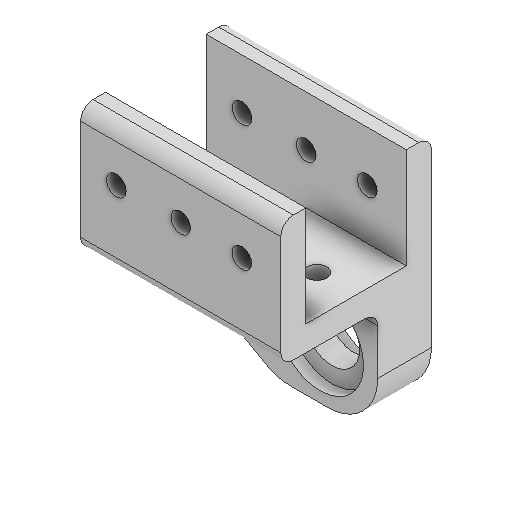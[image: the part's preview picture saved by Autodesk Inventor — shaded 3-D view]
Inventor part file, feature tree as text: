
AUTODESK INVENTOR PART (.ipt)
format: ipt  version: 2025 (Build 290162000, 162)  size: 244,736 bytes
history: native  units: in
note: dims shown in document units (in); Inventor stores cm internally (conversion verified against a paired STEP export)
features: extrude x8, sketch x8, projected_geometry x5, fillet x3
ambient origin geometry x8: Origin, YZ Plane, XZ Plane, XY Plane, X Axis, Y Axis, Z Axis, Center Point
bodies: Solid1 (feature_tree)
feature tree (24):
  extrude  "Extrusion1"  Depth=0.25in
  extrude  "Extrusion2"  Depth=2.0in
  extrude  "Extrusion3"  Depth=0.8661in
  extrude  "Extrusion4"  Depth=0.1969in
  extrude  "Extrusion5"  Depth=0.1969in
  extrude  "Extrusion7"  Depth=0.1969in
  extrude  "Extrusion8"  Depth=0.8661in
  fillet  "Fillet1"  Radius=0.1181in
  extrude  "Extrusion9"  TaperAngle=0.0deg  [1 undecoded]
  fillet  "Fillet2"  Radius=0.5in
  fillet  "Fillet3"  Radius=0.1969in
  sketch  "Sketch1"  dims[d1=1.005in d2=0.25in]
  sketch  "Sketch2"  dims[d3=2.0in d4=0.0in d5=0.5512in]
  projected_geometry  "Projected Loop1"
  sketch  "Sketch3"  dims[d6=0.0in d7=0.0in d8=0.8661in]
  sketch  "Sketch4"  dims[d9=0.1969in d10=0.0in d11=0.1969in]
  projected_geometry  "Projected Loop2"
  sketch  "Sketch5"  dims[d12=0.1969in d13=0.1969in]
  projected_geometry  "Projected Loop3"
  sketch  "Sketch7"  dims[d14=0.2756in d15=0.0in d16=0.1969in]
  sketch  "Sketch8"  dims[d17=0.0in d18=0.0in d21=0.8661in d22=0.1181in d23=0.0in]
  projected_geometry  "Projected Loop5"
  sketch  "Sketch9"  dims[d24=0.1969in d25=0.0in d26=0.0in d27=0.5in d28=0.1969in d29=0.0in d30=0.125in d31=0.125in]
  projected_geometry  "Projected Loop6"
note: 1 required parameter value undecoded (feature->parameter linkage not recoverable at this tier; creation-order binding heuristic only, values carry confidence <= 0.55)
